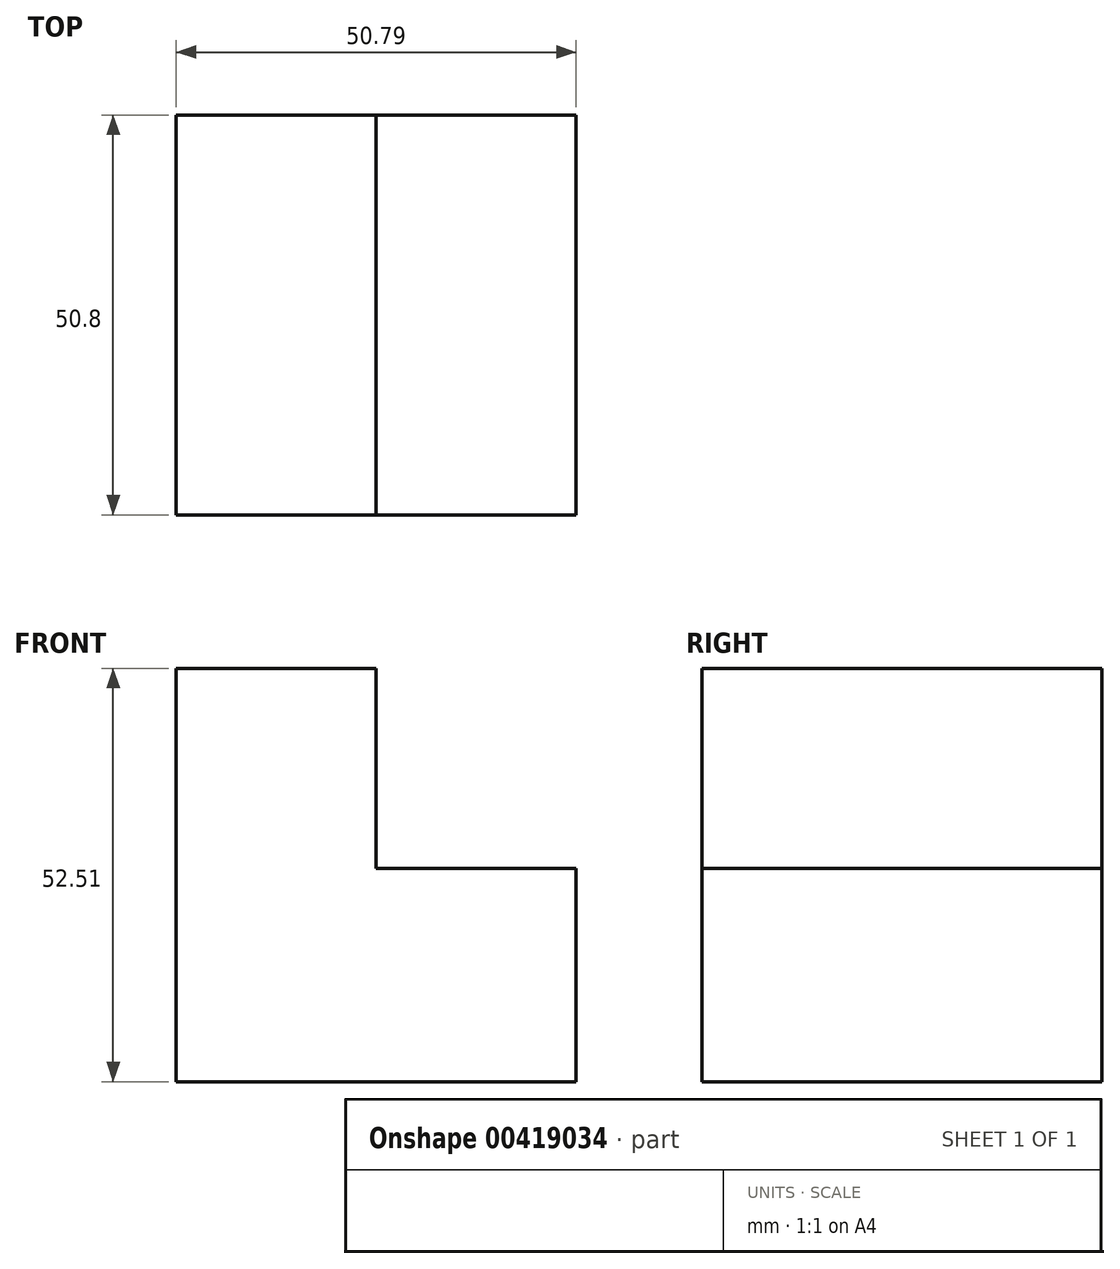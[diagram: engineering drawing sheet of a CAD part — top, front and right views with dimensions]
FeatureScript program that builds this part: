
annotation { "Feature Type Name" : "Feature", "Feature Type Description" : "" }
export const myFeature = defineFeature(function(context is Context, id is Id, definition is map)
    precondition{}
    {
        {
            var Q0;
            Q0=qCreatedBy(makeId("Front.planeOp"),FACE);
            var sketch = newSketch(context, id + "F0", { "sketchPlane" : qUnion([Q0])});
            skLineSegment(sketch, "E0", {"start": v(0, 0) * mm, "end": v(-50.8, 0) * mm});
            skLineSegment(sketch, "E1", {"start": v(-50.8, 1.72) * mm, "end": v(-50.8, 52.51) * mm});
            skLineSegment(sketch, "E2", {"start": v(-50.8, 52.51) * mm, "end": v(-25.38, 52.51) * mm});
            skLineSegment(sketch, "E3", {"start": v(-25.38, 52.51) * mm, "end": v(-25.38, 27.12) * mm});
            skLineSegment(sketch, "E4", {"start": v(-25.38, 27.12) * mm, "end": v(0, 27.12) * mm});
            skLineSegment(sketch, "E5", {"start": v(0, 0) * mm, "end": v(0, 27.12) * mm});
            skLineSegment(sketch, "E6", {"start": v(-50.8, 1.72) * mm, "end": v(-50.8, 0) * mm});
            skSolve(sketch);
        }
        {
            var Q0;
            Q0 = qSketchRegion(id + "F0", true);
            extrude(context, id + "F1", {"entities" : qUnion([Q0]), "depth" : 50.8 * mm});
        }
    });
